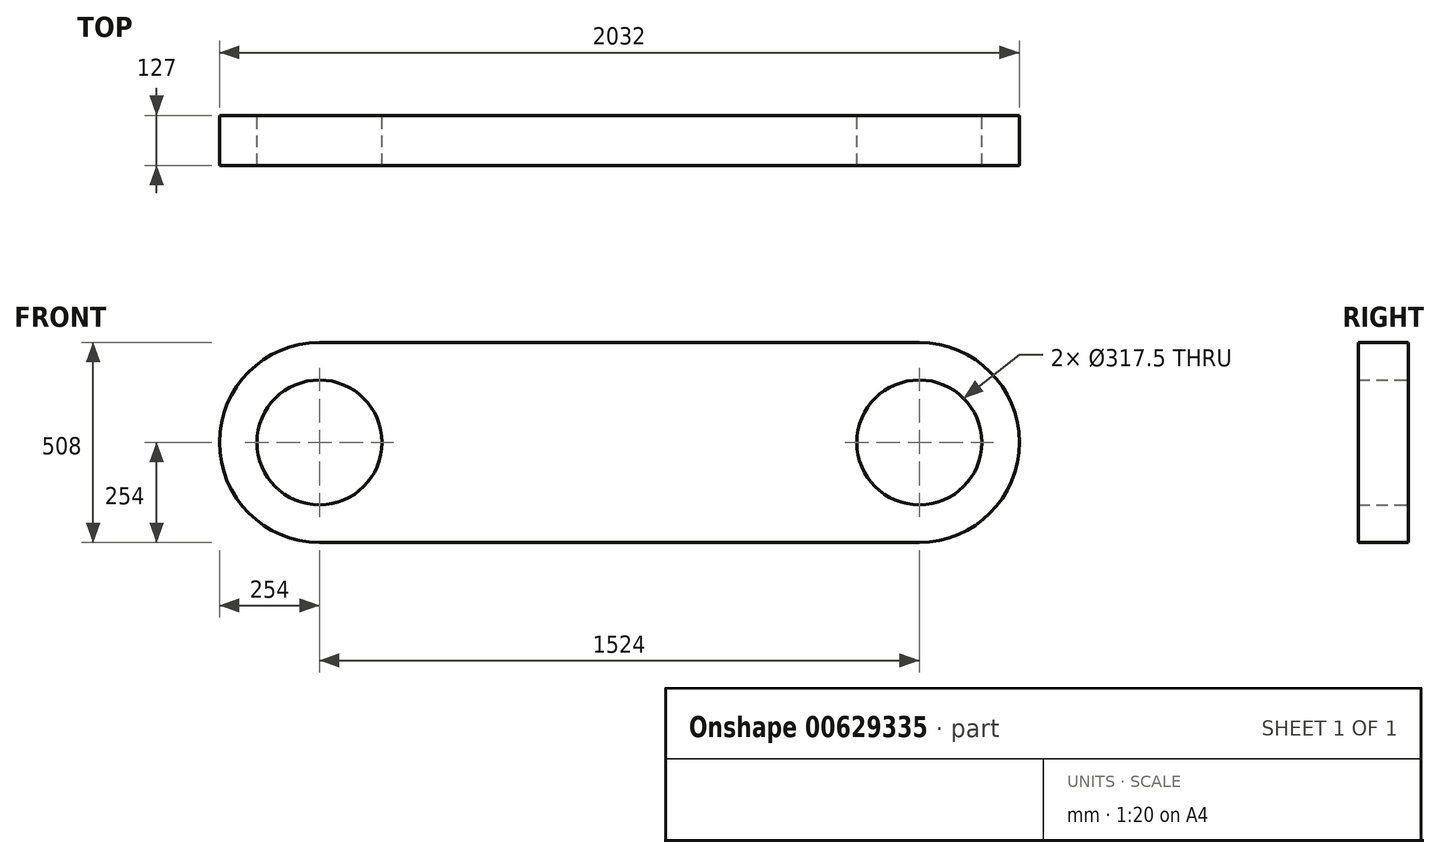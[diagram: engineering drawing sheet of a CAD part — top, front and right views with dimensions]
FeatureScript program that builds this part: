
annotation { "Feature Type Name" : "Feature", "Feature Type Description" : "" }
export const myFeature = defineFeature(function(context is Context, id is Id, definition is map)
    precondition{}
    {
        {
            var Q0;
            Q0=qCreatedBy(makeId("Front.planeOp"),FACE);
            var sketch = newSketch(context, id + "F0", { "sketchPlane" : qUnion([Q0])});
            skLineSegment(sketch, "E0.bottom", {"start": v(-762, 254) * mm, "end": v(762, 254) * mm});
            skLineSegment(sketch, "E0.top", {"start": v(-762, -254) * mm, "end": v(762, -254) * mm});
            skArc(sketch, "E1", {"start": v(-762, 254) * mm, "mid": v(-1016, 0) * mm, "end": v(-762, -254) * mm});
            skArc(sketch, "E2", {"start": v(762, -254) * mm, "mid": v(1016, 0) * mm, "end": v(762, 254) * mm});
            skCircle(sketch, "E3", {"center": v(-762, 0) * mm, "radius": 158.75 * mm});
            skCircle(sketch, "E4", {"center": v(762, 0) * mm, "radius": 158.75 * mm});
            skSolve(sketch);
        }
        {
            var Q0;
            Q0 = qSketchRegion(id + "F0", true);
            extrude(context, id + "F1", {"entities" : qUnion([Q0]), "depth" : 127 * mm, "offsetDistance" : 25.4 * mm});
        }
    });
